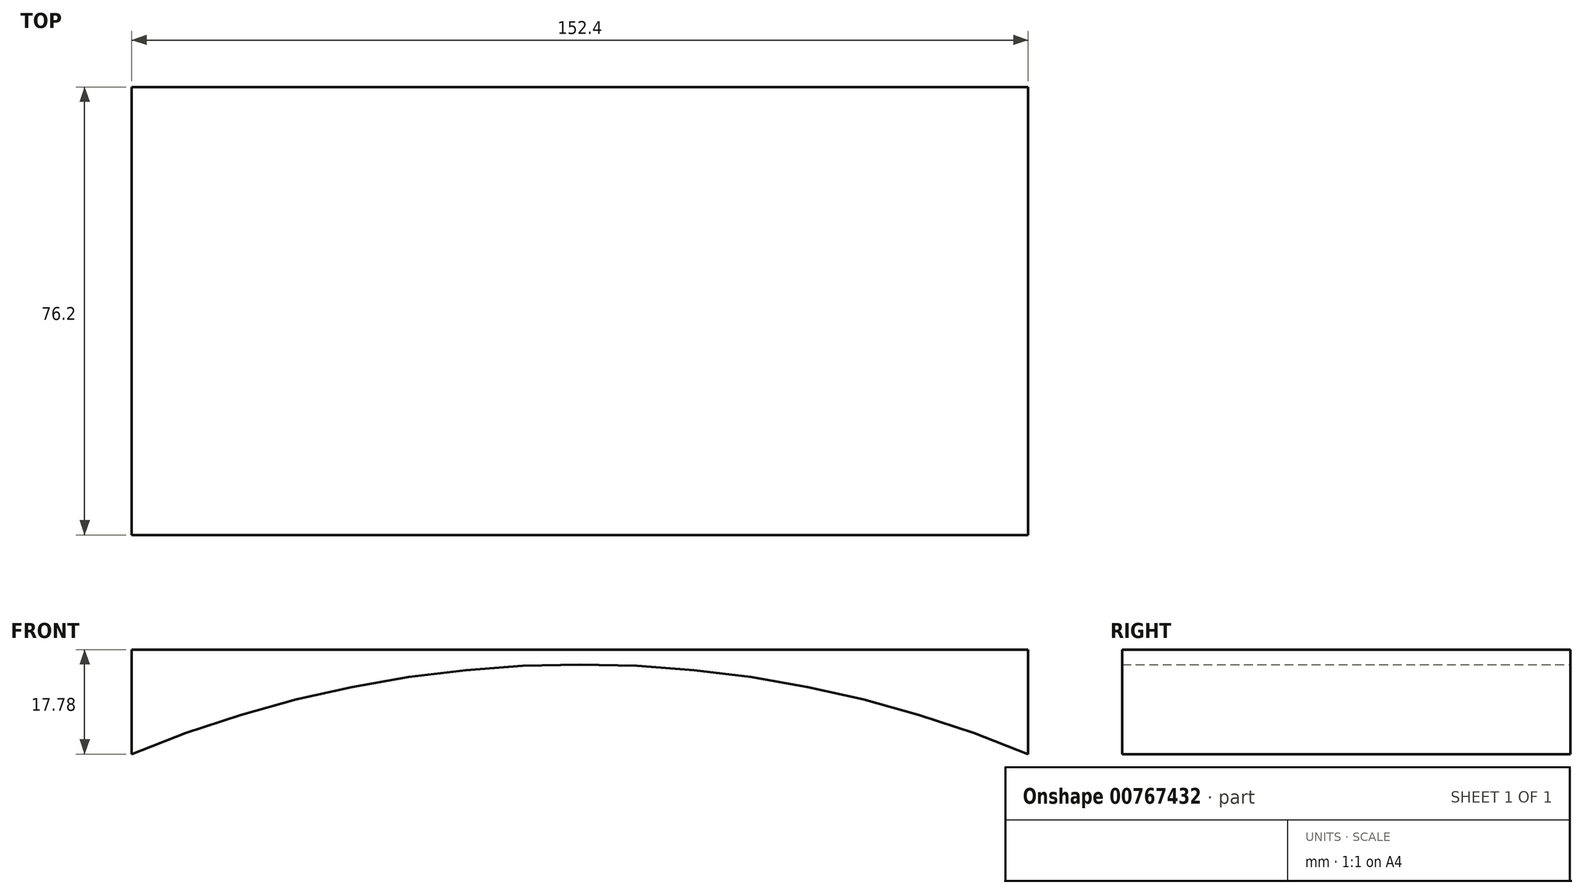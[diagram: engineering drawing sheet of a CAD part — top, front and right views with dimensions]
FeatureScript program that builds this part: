
annotation { "Feature Type Name" : "Feature", "Feature Type Description" : "" }
export const myFeature = defineFeature(function(context is Context, id is Id, definition is map)
    precondition{}
    {
        {
            var Q0;
            Q0=qCreatedBy(makeId("Front.planeOp"),FACE);
            var sketch = newSketch(context, id + "F0", { "sketchPlane" : qUnion([Q0])});
            skArc(sketch, "E0", {"start": v(16.27, 0) * mm, "mid": v(-59.93, 15.24) * mm, "end": v(-136.13, 0) * mm});
            skArc(sketch, "E1", {"start": v(16.27, 0) * mm, "mid": v(28.97, -1.52) * mm, "end": v(41.67, 0) * mm});
            skLineSegment(sketch, "E2", {"start": v(-136.13, 0) * mm, "end": v(-136.13, 17.78) * mm});
            skLineSegment(sketch, "E3", {"start": v(-136.13, 17.78) * mm, "end": v(41.67, 17.78) * mm});
            skLineSegment(sketch, "E4", {"start": v(41.67, 17.78) * mm, "end": v(41.67, 0) * mm});
            skLineSegment(sketch, "E5", {"start": v(16.27, 0) * mm, "end": v(16.27, 50.8) * mm});
            skSolve(sketch);
        }
        {
            var Q0;
            Q0=makeQuery(id+"F0.imprint","IMPRINT",FACE,{"disambiguationData":[TD([[makeQuery(id+"F0.imprint","IMPRINT",EDGE,{"derivedFrom":sQuery(id+"F0.wireOp",EDGE,"E0")}),-1.0]])]});
            extrude(context, id + "F1", {"entities" : qUnion([Q0]), "depth" : 76.2 * mm, "offsetDistance" : 25.4 * mm});
        }
    });
